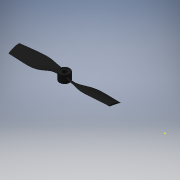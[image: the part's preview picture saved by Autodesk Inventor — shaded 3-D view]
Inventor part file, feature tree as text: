
AUTODESK INVENTOR PART (.ipt)
format: ipt  version: 2019 (Build 230136000, 136)  size: 683,520 bytes
history: native  units: in
note: dims shown in document units (in); Inventor stores cm internally (conversion verified against a paired STEP export)
features: other x3, sketch x2, imported_body x1, extrude x1
ambient origin geometry x8: Origin, YZ Plane, XZ Plane, XY Plane, X Axis, Y Axis, Z Axis, Center Point
bodies: Body1 (feature_tree), Body2 (feature_tree), Body3 (feature_tree)
feature tree (7):
  other  "PROPELLERS"
  imported_body  "Base1"
  sketch  "Sketch1"  dims[d0=5.1181in d1=0.0in]
  extrude  "Extrusion1"  [1 undecoded]
  sketch  "Sketch2"
  other  "Composite1"
  other  "Srf1"
note: 1 required parameter value undecoded (feature->parameter linkage not recoverable at this tier; creation-order binding heuristic only, values carry confidence <= 0.55)
